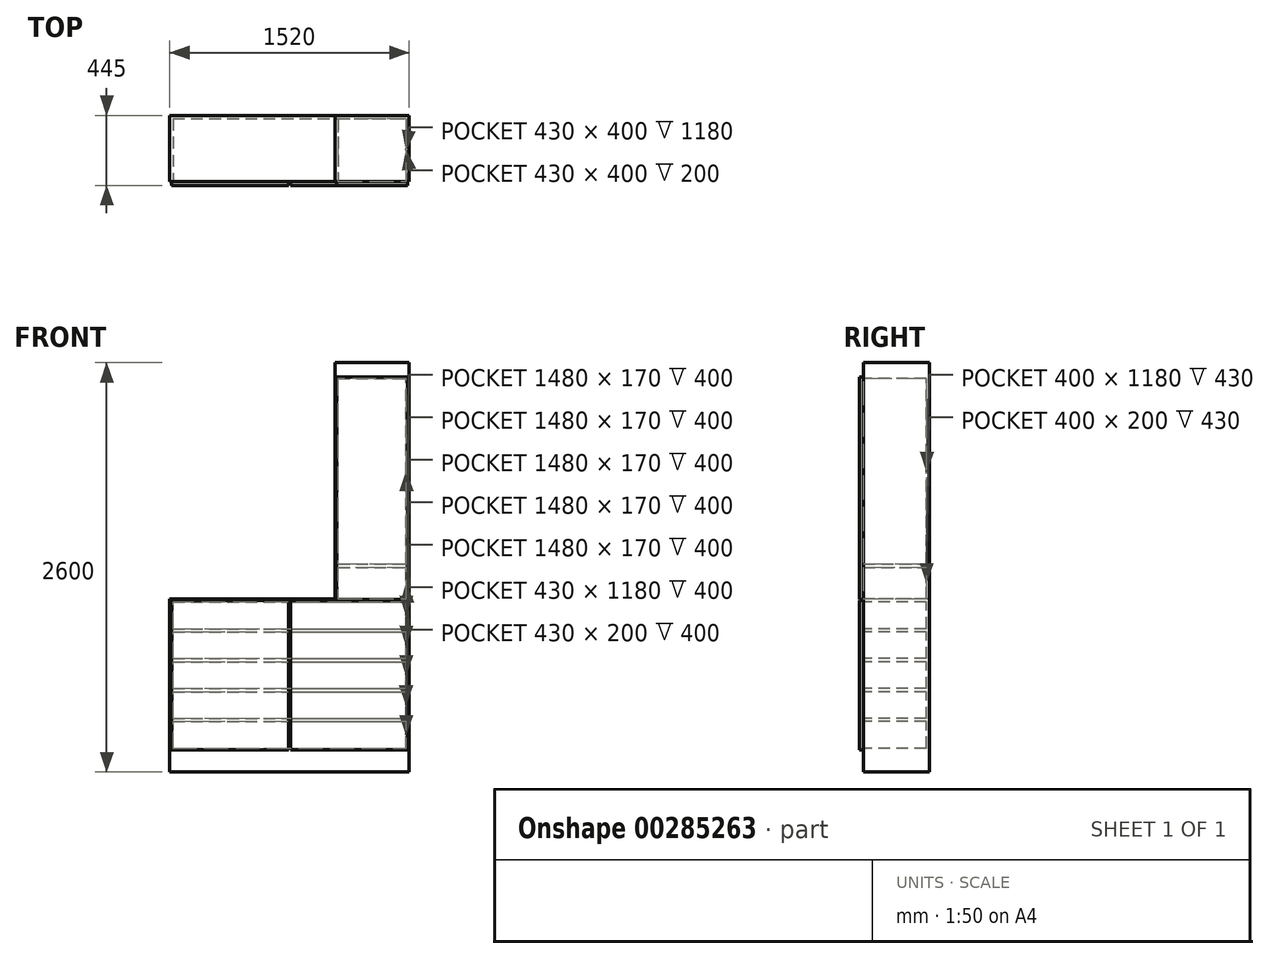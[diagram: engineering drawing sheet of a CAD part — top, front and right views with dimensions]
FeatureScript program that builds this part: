
annotation { "Feature Type Name" : "Feature", "Feature Type Description" : "" }
export const myFeature = defineFeature(function(context is Context, id is Id, definition is map)
    precondition{}
    {
        {
            var Q0;
            Q0=qCreatedBy(makeId("Top.planeOp"),FACE);
            var sketch = newSketch(context, id + "F0", { "sketchPlane" : qUnion([Q0])});
            skLineSegment(sketch, "E0.bottom", {"start": v(0, 0) * mm, "end": v(1520, 0) * mm});
            skLineSegment(sketch, "E0.top", {"start": v(0, 420) * mm, "end": v(1520, 420) * mm});
            skLineSegment(sketch, "E0.left", {"start": v(0, 0) * mm, "end": v(0, 420) * mm});
            skLineSegment(sketch, "E0.right", {"start": v(1520, 0) * mm, "end": v(1520, 420) * mm});
            skSolve(sketch);
        }
        {
            var Q0;
            Q0 = qSketchRegion(id + "F0", true);
            extrude(context, id + "F1", {"entities" : qUnion([Q0]), "depth" : 2600 * mm});
        }
        {
            var Q0;
            Q0=makeQuery(id+"F1.opExtrude","SWEPT_FACE",FACE,{"disambiguationData":[OSD([sQuery(id+"F0.wireOp",EDGE,"E0.bottom")])]});
            var sketch = newSketch(context, id + "F2", { "sketchPlane" : qUnion([Q0])});
            skLineSegment(sketch, "E1.bottom", {"start": v(0, 2600) * mm, "end": v(1050, 2600) * mm});
            skLineSegment(sketch, "E1.top", {"start": v(0, 1100) * mm, "end": v(1050, 1100) * mm});
            skLineSegment(sketch, "E1.left", {"start": v(0, 2600) * mm, "end": v(0, 1100) * mm});
            skLineSegment(sketch, "E1.right", {"start": v(1050, 2600) * mm, "end": v(1050, 1100) * mm});
            skSolve(sketch);
        }
        {
            var Q0;
            Q0 = qSketchRegion(id + "F2", true);
            extrude(context, id + "F3", {"entities" : qUnion([Q0]), "operationType" : NewBodyOperationType.REMOVE, "endBound" : BoundingType.THROUGH_ALL, "oppositeDirection" : true, "depth" : 25 * mm});
        }
        {
            var Q0;
            Q0=makeQuery(id+"F1.opExtrude","SWEPT_FACE",FACE,{"disambiguationData":[OSD([sQuery(id+"F0.wireOp",EDGE,"E0.top")])]});
            cPlane(context, id + "F4", {"entities" : qUnion([Q0]), "cplaneType" : CPlaneType.OFFSET, "offset" : 20 * mm, "oppositeDirection" : true, "width" : 150 * mm, "height" : 150 * mm});
        }
        {
            var Q0;
            Q0=makeQuery(id+"F1.opExtrude","SWEPT_FACE",FACE,{"disambiguationData":[OSD([sQuery(id+"F0.wireOp",EDGE,"E0.bottom")])]});
            var sketch = newSketch(context, id + "F5", { "sketchPlane" : qUnion([Q0])});
            skLineSegment(sketch, "E2.bottom", {"start": v(1070, 1100) * mm, "end": v(1500, 1100) * mm});
            skLineSegment(sketch, "E2.top", {"start": v(1070, 2500) * mm, "end": v(1500, 2500) * mm});
            skLineSegment(sketch, "E2.left", {"start": v(1070, 1100) * mm, "end": v(1070, 2500) * mm});
            skLineSegment(sketch, "E2.right", {"start": v(1500, 1100) * mm, "end": v(1500, 2500) * mm});
            skSolve(sketch);
        }
        {
            var Q0;
            Q0 = qSketchRegion(id + "F5", true);
            var Q1;
            Q1=qCreatedBy(id+"F4.planeOp",FACE);
            extrude(context, id + "F6", {"entities" : qUnion([Q0]), "operationType" : NewBodyOperationType.REMOVE, "endBound" : BoundingType.UP_TO_SURFACE, "oppositeDirection" : true, "endBoundEntityFace" : qUnion([Q1]), "depth" : 25 * mm});
        }
        {
            var Q0;
            Q0=makeQuery(id+"F1.opExtrude","SWEPT_FACE",FACE,{"disambiguationData":[OSD([sQuery(id+"F0.wireOp",EDGE,"E0.bottom")])]});
            var sketch = newSketch(context, id + "F7", { "sketchPlane" : qUnion([Q0])});
            skLineSegment(sketch, "E3.bottom", {"start": v(20, 150) * mm, "end": v(1500, 150) * mm});
            skLineSegment(sketch, "E3.top", {"start": v(20, 320) * mm, "end": v(1500, 320) * mm});
            skLineSegment(sketch, "E3.left", {"start": v(20, 150) * mm, "end": v(20, 320) * mm});
            skLineSegment(sketch, "E3.right", {"start": v(1500, 150) * mm, "end": v(1500, 320) * mm});
            skLineSegment(sketch, "E4.bottom", {"start": v(20, 910) * mm, "end": v(1500, 910) * mm});
            skLineSegment(sketch, "E4.top", {"start": v(20, 1080) * mm, "end": v(1500, 1080) * mm});
            skLineSegment(sketch, "E4.left", {"start": v(20, 910) * mm, "end": v(20, 1080) * mm});
            skLineSegment(sketch, "E4.right", {"start": v(1500, 910) * mm, "end": v(1500, 1080) * mm});
            skLineSegment(sketch, "E5.0.1.0", {"start": v(20, 340) * mm, "end": v(20, 510) * mm});
            skLineSegment(sketch, "E5.0.1.1", {"start": v(1500, 340) * mm, "end": v(1500, 510) * mm});
            skLineSegment(sketch, "E5.0.1.2", {"start": v(20, 510) * mm, "end": v(1500, 510) * mm});
            skLineSegment(sketch, "E5.0.1.3", {"start": v(20, 340) * mm, "end": v(1500, 340) * mm});
            skLineSegment(sketch, "E5.0.2.0", {"start": v(20, 530) * mm, "end": v(20, 700) * mm});
            skLineSegment(sketch, "E5.0.2.1", {"start": v(1500, 530) * mm, "end": v(1500, 700) * mm});
            skLineSegment(sketch, "E5.0.2.2", {"start": v(20, 700) * mm, "end": v(1500, 700) * mm});
            skLineSegment(sketch, "E5.0.2.3", {"start": v(20, 530) * mm, "end": v(1500, 530) * mm});
            skLineSegment(sketch, "E5.0.3.0", {"start": v(20, 720) * mm, "end": v(20, 890) * mm});
            skLineSegment(sketch, "E5.0.3.1", {"start": v(1500, 720) * mm, "end": v(1500, 890) * mm});
            skLineSegment(sketch, "E5.0.3.2", {"start": v(20, 890) * mm, "end": v(1500, 890) * mm});
            skLineSegment(sketch, "E5.0.3.3", {"start": v(20, 720) * mm, "end": v(1500, 720) * mm});
            skLineSegment(sketch, "E5.direction1", {"start": v(20, 150) * mm, "end": v(45, 150) * mm, "construction": true});
            skLineSegment(sketch, "E5.direction2", {"start": v(20, 150) * mm, "end": v(20, 340) * mm, "construction": true});
            skSolve(sketch);
        }
        {
            var Q0;
            Q0 = qSketchRegion(id + "F7", true);
            var Q1;
            Q1=qCreatedBy(id+"F4.planeOp",FACE);
            extrude(context, id + "F8", {"entities" : qUnion([Q0]), "operationType" : NewBodyOperationType.REMOVE, "endBound" : BoundingType.UP_TO_SURFACE, "oppositeDirection" : true, "endBoundEntityFace" : qUnion([Q1]), "depth" : 25 * mm});
        }
        {
            var Q0;
            Q0=qCreatedBy(makeId("Front.planeOp"),FACE);
            var sketch = newSketch(context, id + "F9", { "sketchPlane" : qUnion([Q0])});
            skLineSegment(sketch, "E6.bottom", {"start": v(10, 1090) * mm, "end": v(755.69, 1090) * mm});
            skLineSegment(sketch, "E6.top", {"start": v(10, 140) * mm, "end": v(755.69, 140) * mm});
            skLineSegment(sketch, "E6.left", {"start": v(10, 1090) * mm, "end": v(10, 140) * mm});
            skLineSegment(sketch, "E6.right", {"start": v(755.69, 1090) * mm, "end": v(755.69, 140) * mm});
            skLineSegment(sketch, "E7.bottom", {"start": v(765.69, 1090) * mm, "end": v(1510, 1090) * mm});
            skLineSegment(sketch, "E7.top", {"start": v(765.69, 140) * mm, "end": v(1510, 140) * mm});
            skLineSegment(sketch, "E7.left", {"start": v(765.69, 1090) * mm, "end": v(765.69, 140) * mm});
            skLineSegment(sketch, "E7.right", {"start": v(1510, 1090) * mm, "end": v(1510, 140) * mm});
            skPoint(sketch, "E8.orphan", {"position": v(0, 1090) * mm});
            skLineSegment(sketch, "E9", {"start": v(760, 1378.24) * mm, "end": v(760, -91.27) * mm, "construction": true});
            skLineSegment(sketch, "E10.bottom", {"start": v(1060, 2510) * mm, "end": v(1510, 2510) * mm});
            skLineSegment(sketch, "E10.top", {"start": v(1060, 1095) * mm, "end": v(1510, 1095) * mm});
            skLineSegment(sketch, "E10.left", {"start": v(1060, 2510) * mm, "end": v(1060, 1095) * mm});
            skLineSegment(sketch, "E10.right", {"start": v(1510, 2510) * mm, "end": v(1510, 1095) * mm});
            skSolve(sketch);
        }
        {
            var Q0;
            Q0 = qSketchRegion(id + "F9", true);
            extrude(context, id + "F10", {"entities" : qUnion([Q0]), "depth" : 25 * mm});
        }
        {
            var Q0;
            Q0=qCreatedBy(id+"F4.planeOp",FACE);
            var sketch = newSketch(context, id + "F11", { "sketchPlane" : qUnion([Q0])});
            skLineSegment(sketch, "E11.bottom", {"start": v(-1070, 1320) * mm, "end": v(-1500, 1320) * mm});
            skLineSegment(sketch, "E11.top", {"start": v(-1070, 1300) * mm, "end": v(-1500, 1300) * mm});
            skLineSegment(sketch, "E11.left", {"start": v(-1070, 1320) * mm, "end": v(-1070, 1300) * mm});
            skLineSegment(sketch, "E11.right", {"start": v(-1500, 1320) * mm, "end": v(-1500, 1300) * mm});
            skSolve(sketch);
        }
        {
            var Q0;
            Q0 = qSketchRegion(id + "F11", true);
            var Q1;
            Q1=makeQuery(id+"F1.opExtrude","SWEPT_FACE",FACE,{"disambiguationData":[OSD([sQuery(id+"F0.wireOp",EDGE,"E0.bottom")])]});
            extrude(context, id + "F12", {"entities" : qUnion([Q0]), "operationType" : NewBodyOperationType.ADD, "endBound" : BoundingType.UP_TO_SURFACE, "oppositeDirection" : true, "endBoundEntityFace" : qUnion([Q1]), "depth" : 25 * mm});
        }
    });
